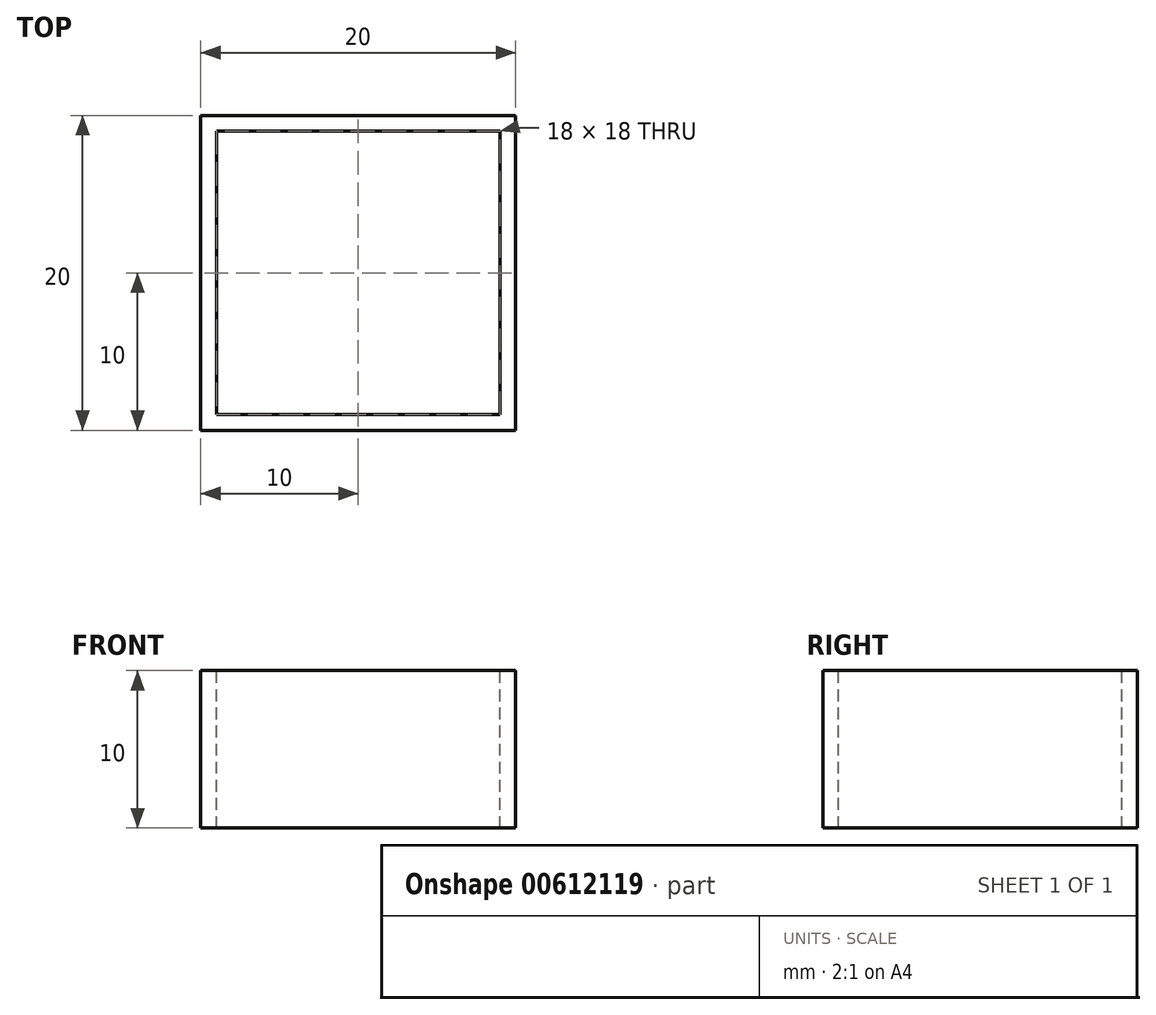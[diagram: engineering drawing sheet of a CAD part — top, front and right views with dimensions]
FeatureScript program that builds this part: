
annotation { "Feature Type Name" : "Feature", "Feature Type Description" : "" }
export const myFeature = defineFeature(function(context is Context, id is Id, definition is map)
    precondition{}
    {
        {
            var Q0;
            Q0=qCreatedBy(makeId("Top.planeOp"),FACE);
            var sketch = newSketch(context, id + "F0", { "sketchPlane" : qUnion([Q0])});
            skLineSegment(sketch, "E0.bottom", {"start": v(-10, -10) * mm, "end": v(10, -10) * mm});
            skLineSegment(sketch, "E0.top", {"start": v(-10, 10) * mm, "end": v(10, 10) * mm});
            skLineSegment(sketch, "E0.left", {"start": v(-10, -10) * mm, "end": v(-10, 10) * mm});
            skLineSegment(sketch, "E0.right", {"start": v(10, -10) * mm, "end": v(10, 10) * mm});
            skLineSegment(sketch, "E1", {"start": v(-10, 0) * mm, "end": v(10, 0) * mm, "construction": true});
            skSolve(sketch);
        }
        {
            var Q0;
            Q0 = qSketchRegion(id + "F0", true);
            extrude(context, id + "F1", {"entities" : qUnion([Q0]), "depth" : 10 * mm, "offsetDistance" : 25 * mm});
        }
        {
            var Q0;
            Q0=makeQuery(id+"F1.opExtrude","CAP_FACE",FACE,{"disambiguationData":[OSD([sQuery(id+"F0.wireOp",EDGE,"E0.bottom"),sQuery(id+"F0.wireOp",EDGE,"E0.top"),sQuery(id+"F0.wireOp",EDGE,"E0.left"),sQuery(id+"F0.wireOp",EDGE,"E0.right")])],"isStart":false});
            var sketch = newSketch(context, id + "F2", { "sketchPlane" : qUnion([Q0])});
            skLineSegment(sketch, "E2.0", {"start": v(-10, 10) * mm, "end": v(10, 10) * mm, "construction": true});
            skLineSegment(sketch, "E3.0", {"start": v(-10, -10) * mm, "end": v(-10, 10) * mm, "construction": true});
            skLineSegment(sketch, "E4.0", {"start": v(-10, -10) * mm, "end": v(10, -10) * mm, "construction": true});
            skLineSegment(sketch, "E5.0", {"start": v(10, -10) * mm, "end": v(10, 10) * mm, "construction": true});
            skLineSegment(sketch, "E6.0", {"start": v(-9, 9) * mm, "end": v(9, 9) * mm});
            skLineSegment(sketch, "E6.1", {"start": v(-9, -9) * mm, "end": v(-9, 9) * mm});
            skLineSegment(sketch, "E6.2", {"start": v(-9, -9) * mm, "end": v(9, -9) * mm});
            skLineSegment(sketch, "E6.3", {"start": v(9, -9) * mm, "end": v(9, 9) * mm});
            skSolve(sketch);
        }
        {
            var Q0;
            Q0 = qSketchRegion(id + "F2", true);
            extrude(context, id + "F3", {"entities" : qUnion([Q0]), "operationType" : NewBodyOperationType.REMOVE, "endBound" : BoundingType.THROUGH_ALL, "oppositeDirection" : true, "depth" : 25 * mm, "offsetDistance" : 25 * mm});
        }
    });
